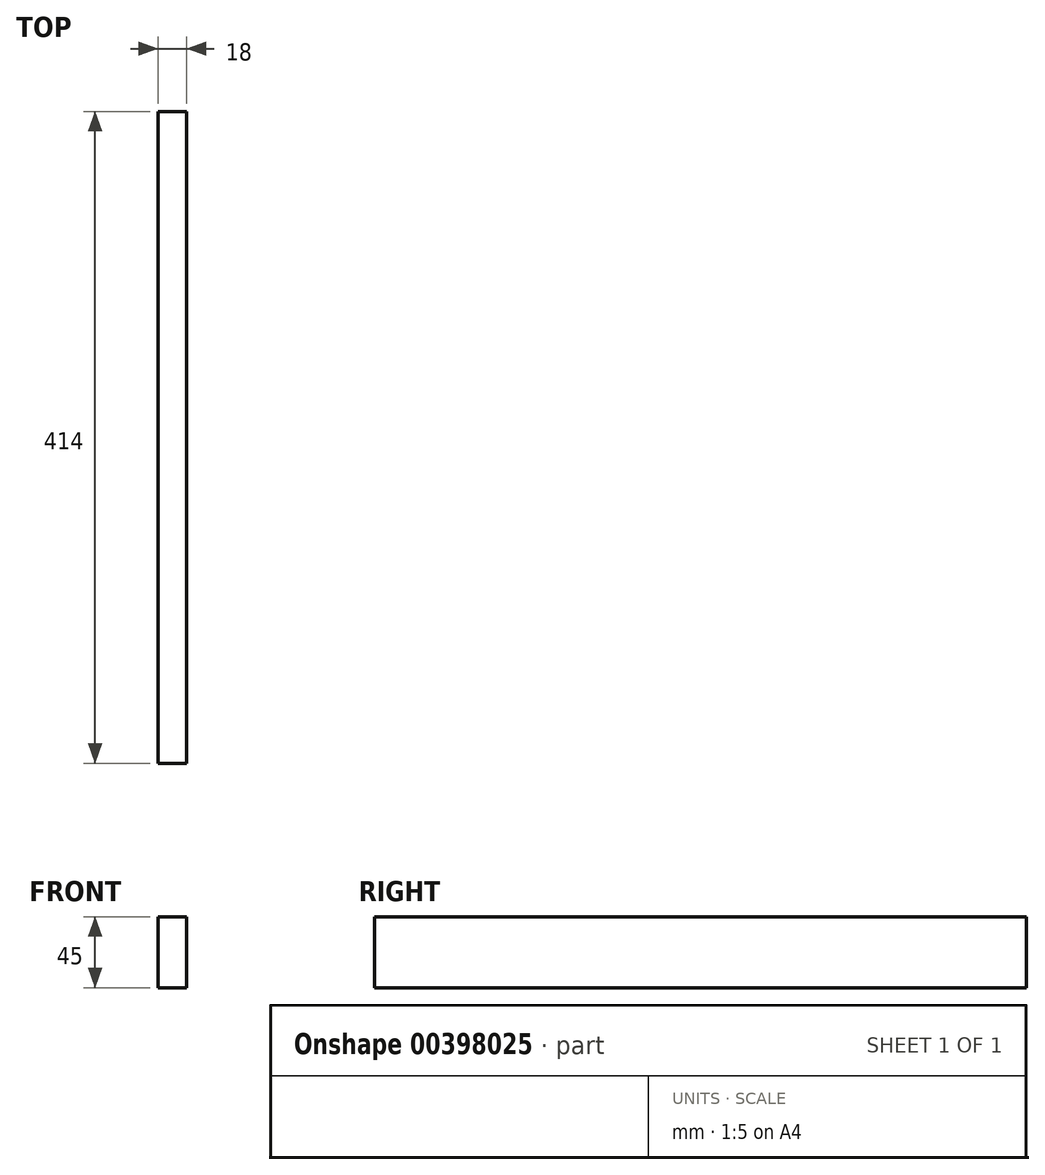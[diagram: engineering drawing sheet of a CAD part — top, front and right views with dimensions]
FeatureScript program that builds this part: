
annotation { "Feature Type Name" : "Feature", "Feature Type Description" : "" }
export const myFeature = defineFeature(function(context is Context, id is Id, definition is map)
    precondition{}
    {
        {
            var Q0;
            Q0=qCreatedBy(makeId("Right.planeOp"),FACE);
            var sketch = newSketch(context, id + "F0", { "sketchPlane" : qUnion([Q0])});
            skLineSegment(sketch, "E0.bottom", {"start": v(207, -22.5) * mm, "end": v(-207, -22.5) * mm});
            skLineSegment(sketch, "E0.top", {"start": v(207, 22.5) * mm, "end": v(-207, 22.5) * mm});
            skLineSegment(sketch, "E0.left", {"start": v(207, -22.5) * mm, "end": v(207, 22.5) * mm});
            skLineSegment(sketch, "E0.right", {"start": v(-207, -22.5) * mm, "end": v(-207, 22.5) * mm});
            skPoint(sketch, "E0.middle", {"position": v(0, 0) * mm});
            skSolve(sketch);
        }
        {
            var Q0;
            Q0 = qSketchRegion(id + "F0", true);
            extrude(context, id + "F1", {"entities" : qUnion([Q0]), "depth" : 18 * mm});
        }
    });
